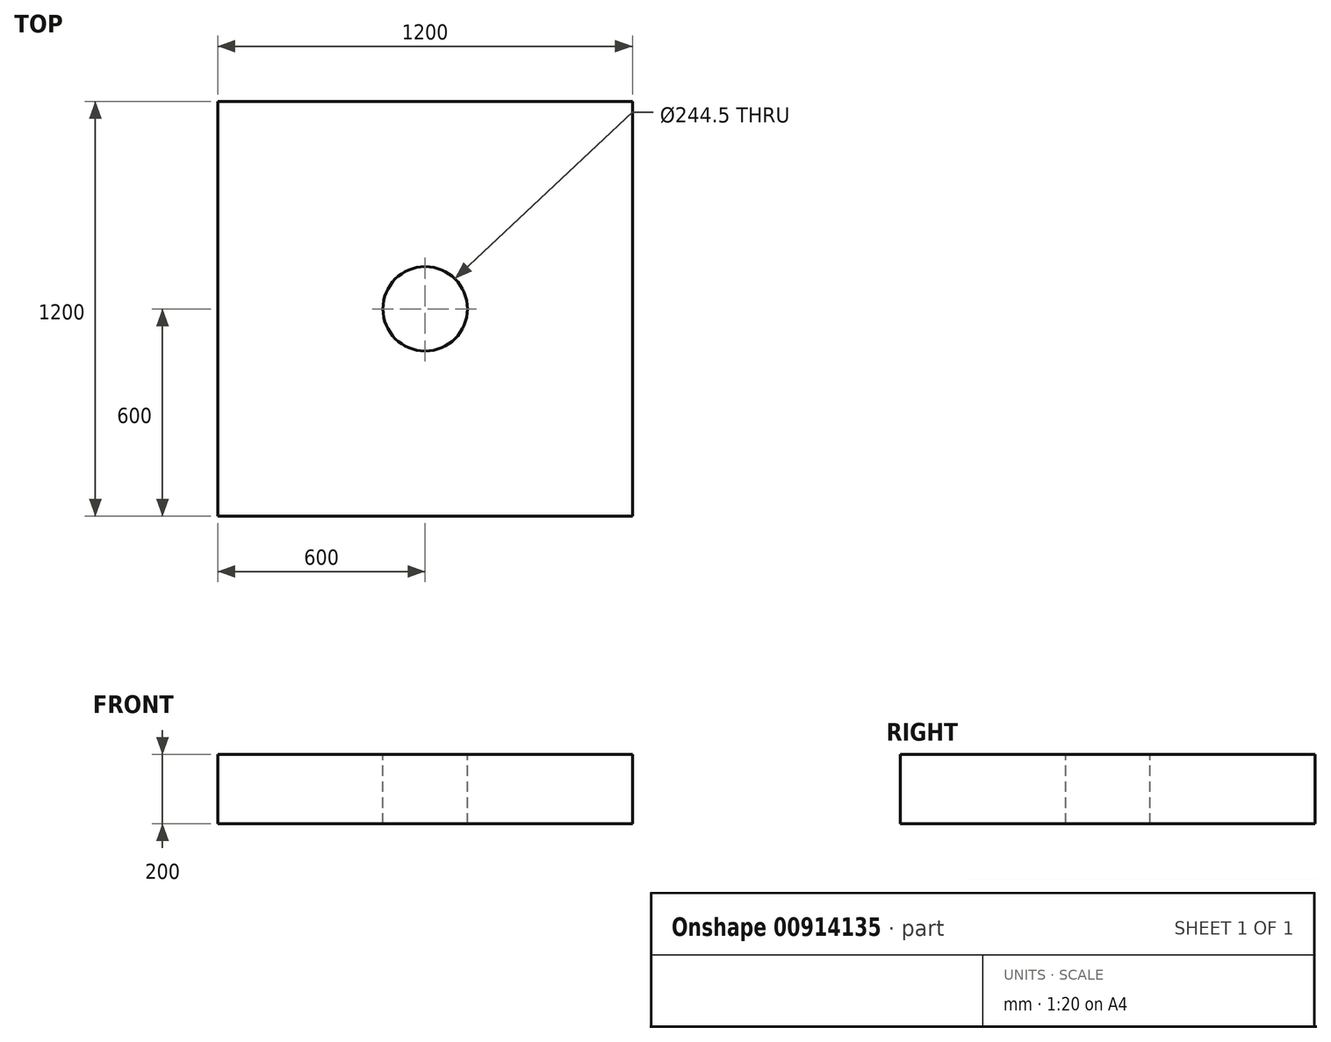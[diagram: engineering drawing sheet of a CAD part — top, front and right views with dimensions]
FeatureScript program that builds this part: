
annotation { "Feature Type Name" : "Feature", "Feature Type Description" : "" }
export const myFeature = defineFeature(function(context is Context, id is Id, definition is map)
    precondition{}
    {
        {
            var Q0;
            Q0=qCreatedBy(makeId("Top.planeOp"),FACE);
            var sketch = newSketch(context, id + "F0", { "sketchPlane" : qUnion([Q0])});
            skLineSegment(sketch, "E0.bottom", {"start": v(600, 600) * mm, "end": v(-600, 600) * mm});
            skLineSegment(sketch, "E0.top", {"start": v(600, -600) * mm, "end": v(-600, -600) * mm});
            skLineSegment(sketch, "E0.left", {"start": v(600, 600) * mm, "end": v(600, -600) * mm});
            skLineSegment(sketch, "E0.right", {"start": v(-600, 600) * mm, "end": v(-600, -600) * mm});
            skPoint(sketch, "E0.middle", {"position": v(0, 0) * mm});
            skCircle(sketch, "E1", {"center": v(0, 0) * mm, "radius": 122.25 * mm});
            skSolve(sketch);
        }
        {
            var Q0;
            Q0=makeQuery(id+"F0.imprint","IMPRINT",FACE,{"disambiguationData":[TD([[makeQuery(id+"F0.imprint","IMPRINT",EDGE,{"derivedFrom":sQuery(id+"F0.wireOp",EDGE,"E0.bottom")}),1.0]])]});
            extrude(context, id + "F1", {"entities" : qUnion([Q0]), "oppositeDirection" : true, "depth" : 200 * mm, "offsetDistance" : 25 * mm});
        }
    });
